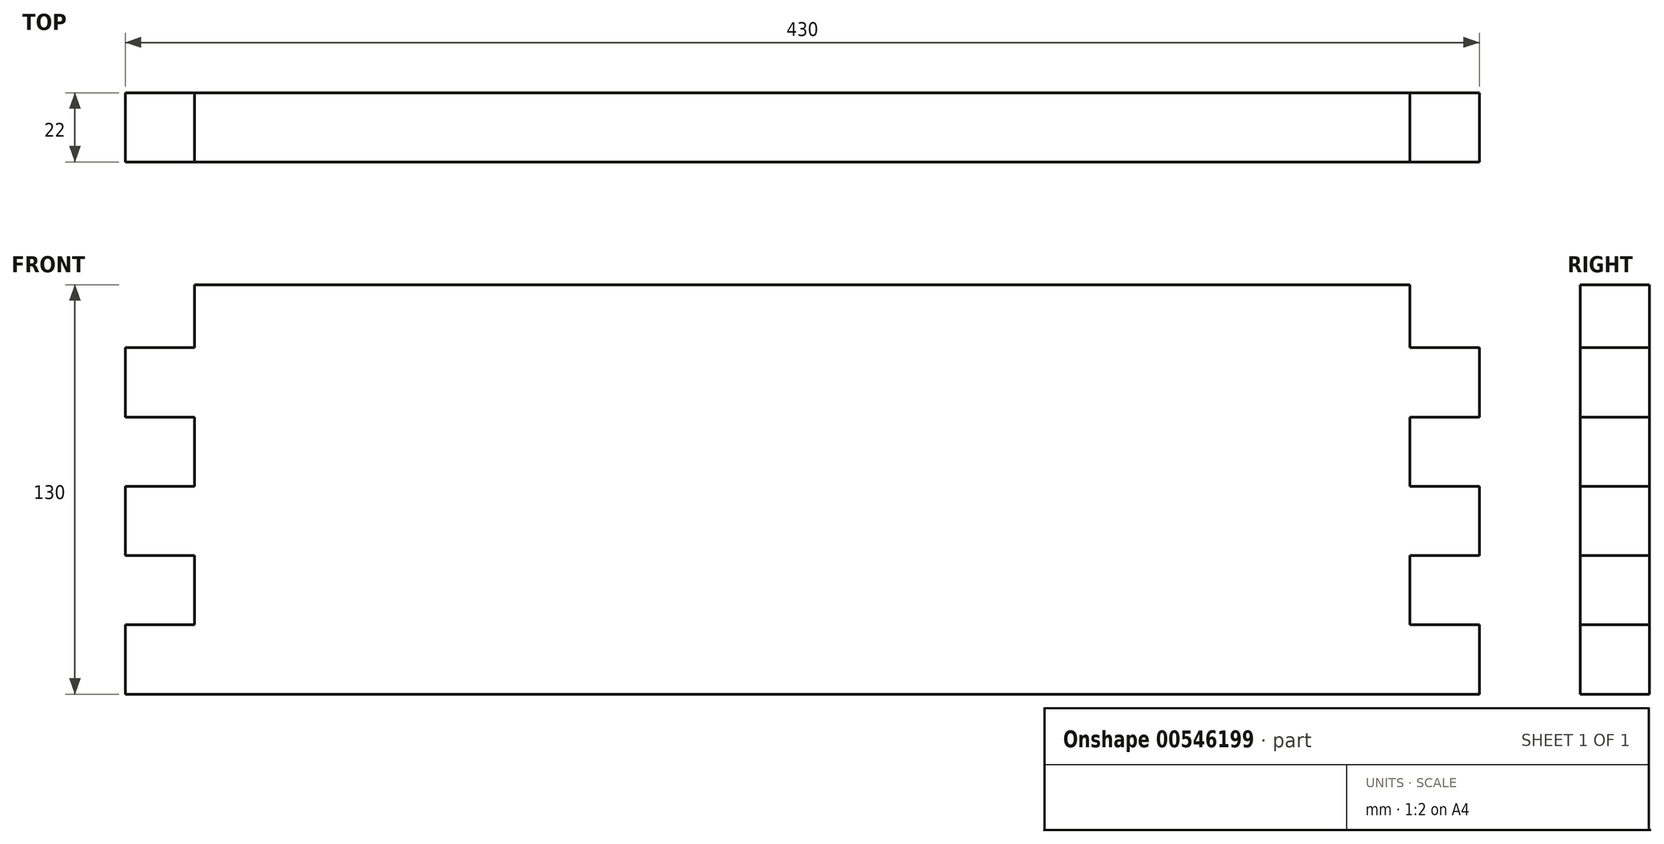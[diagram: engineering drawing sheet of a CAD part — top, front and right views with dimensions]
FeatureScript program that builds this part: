
annotation { "Feature Type Name" : "Feature", "Feature Type Description" : "" }
export const myFeature = defineFeature(function(context is Context, id is Id, definition is map)
    precondition{}
    {
        {
            var Q0;
            Q0=qCreatedBy(makeId("Front.planeOp"),FACE);
            var sketch = newSketch(context, id + "F0", { "sketchPlane" : qUnion([Q0])});
            skLineSegment(sketch, "E0.bottom", {"start": v(0, 0) * mm, "end": v(430, 0) * mm});
            skLineSegment(sketch, "E0.top", {"start": v(0, 130) * mm, "end": v(430, 130) * mm});
            skLineSegment(sketch, "E0.left", {"start": v(0, 0) * mm, "end": v(0, 130) * mm});
            skLineSegment(sketch, "E0.right", {"start": v(430, 0) * mm, "end": v(430, 130) * mm});
            skSolve(sketch);
        }
        {
            var Q0;
            Q0=makeQuery(id+"F0.imprint","IMPRINT",FACE,{"disambiguationData":[TD([[makeQuery(id+"F0.imprint","IMPRINT",EDGE,{"derivedFrom":sQuery(id+"F0.wireOp",EDGE,"E0.bottom")}),1.0]])]});
            extrude(context, id + "F1", {"entities" : qUnion([Q0]), "depth" : 22 * mm, "offsetDistance" : 25 * mm});
        }
        {
            var Q0;
            Q0=makeQuery(id+"F1.opExtrude","CAP_FACE",FACE,{"disambiguationData":[OSD([sQuery(id+"F0.wireOp",EDGE,"E0.bottom"),sQuery(id+"F0.wireOp",EDGE,"E0.top"),sQuery(id+"F0.wireOp",EDGE,"E0.left"),sQuery(id+"F0.wireOp",EDGE,"E0.right")])],"isStart":false});
            var sketch = newSketch(context, id + "F2", { "sketchPlane" : qUnion([Q0])});
            skLineSegment(sketch, "E1", {"start": v(215, 130) * mm, "end": v(215, 0) * mm});
            skLineSegment(sketch, "E2.bottom", {"start": v(0, 0) * mm, "end": v(22, 0) * mm});
            skLineSegment(sketch, "E2.top", {"start": v(0, 22) * mm, "end": v(22, 22) * mm});
            skLineSegment(sketch, "E2.left", {"start": v(0, 0) * mm, "end": v(0, 22) * mm});
            skLineSegment(sketch, "E2.right", {"start": v(22, 0) * mm, "end": v(22, 22) * mm});
            skLineSegment(sketch, "E3.top", {"start": v(0, 44) * mm, "end": v(22, 44) * mm});
            skLineSegment(sketch, "E3.left", {"start": v(0, 22) * mm, "end": v(0, 44) * mm});
            skLineSegment(sketch, "E3.right", {"start": v(22, 22) * mm, "end": v(22, 44) * mm});
            skLineSegment(sketch, "E4.top", {"start": v(0, 66) * mm, "end": v(22, 66) * mm});
            skLineSegment(sketch, "E4.left", {"start": v(0, 44) * mm, "end": v(0, 66) * mm});
            skLineSegment(sketch, "E4.right", {"start": v(22, 44) * mm, "end": v(22, 66) * mm});
            skLineSegment(sketch, "E5.top", {"start": v(0, 88) * mm, "end": v(22, 88) * mm});
            skLineSegment(sketch, "E5.left", {"start": v(0, 66) * mm, "end": v(0, 88) * mm});
            skLineSegment(sketch, "E5.right", {"start": v(22, 66) * mm, "end": v(22, 88) * mm});
            skLineSegment(sketch, "E6.top", {"start": v(0, 110) * mm, "end": v(22, 110) * mm});
            skLineSegment(sketch, "E6.left", {"start": v(0, 88) * mm, "end": v(0, 110) * mm});
            skLineSegment(sketch, "E6.right", {"start": v(22, 88) * mm, "end": v(22, 110) * mm});
            skLineSegment(sketch, "E7.MirrorCS", {"start": v(430, 22) * mm, "end": v(408, 22) * mm});
            skLineSegment(sketch, "E8.MirrorCS", {"start": v(430, 44) * mm, "end": v(408, 44) * mm});
            skLineSegment(sketch, "E9.MirrorCS", {"start": v(430, 66) * mm, "end": v(408, 66) * mm});
            skLineSegment(sketch, "E10.MirrorCS", {"start": v(430, 88) * mm, "end": v(408, 88) * mm});
            skLineSegment(sketch, "E11.MirrorCS", {"start": v(408, 66) * mm, "end": v(408, 88) * mm});
            skLineSegment(sketch, "E12.MirrorCS", {"start": v(408, 0) * mm, "end": v(408, 22) * mm});
            skLineSegment(sketch, "E13.MirrorCS", {"start": v(430, 0) * mm, "end": v(430, 22) * mm});
            skLineSegment(sketch, "E14.MirrorCS", {"start": v(430, 0) * mm, "end": v(408, 0) * mm});
            skLineSegment(sketch, "E15.MirrorCS", {"start": v(430, 22) * mm, "end": v(430, 44) * mm});
            skLineSegment(sketch, "E16.MirrorCS", {"start": v(408, 22) * mm, "end": v(408, 44) * mm});
            skLineSegment(sketch, "E17.MirrorCS", {"start": v(430, 66) * mm, "end": v(430, 88) * mm});
            skLineSegment(sketch, "E18.MirrorCS", {"start": v(430, 44) * mm, "end": v(430, 66) * mm});
            skLineSegment(sketch, "E19.MirrorCS", {"start": v(408, 44) * mm, "end": v(408, 66) * mm});
            skLineSegment(sketch, "E20.MirrorCS", {"start": v(408, 88) * mm, "end": v(408, 110) * mm});
            skLineSegment(sketch, "E21.MirrorCS", {"start": v(430, 110) * mm, "end": v(408, 110) * mm});
            skLineSegment(sketch, "E22.MirrorCS", {"start": v(430, 88) * mm, "end": v(430, 110) * mm});
            skLineSegment(sketch, "E23", {"start": v(22, 110) * mm, "end": v(22, 130) * mm});
            skLineSegment(sketch, "E24", {"start": v(408, 110) * mm, "end": v(408, 130) * mm});
            skSolve(sketch);
        }
        {
            var Q0;
            Q0=makeQuery(id+"F2.imprint","IMPRINT",FACE,{"disambiguationData":[TD([[makeQuery(id+"F2.imprint","IMPRINT",EDGE,{"derivedFrom":sQuery(id+"F2.wireOp",EDGE,"E2.top")}),1.0]])]});
            var Q1;
            Q1=makeQuery(id+"F2.imprint","IMPRINT",FACE,{"disambiguationData":[TD([[makeQuery(id+"F2.imprint","IMPRINT",EDGE,{"derivedFrom":sQuery(id+"F2.wireOp",EDGE,"E4.top")}),1.0]])]});
            var Q2;
            Q2=makeQuery(id+"F2.imprint","IMPRINT",FACE,{"disambiguationData":[TD([[makeQuery(id+"F2.imprint","IMPRINT",EDGE,{"derivedFrom":sQuery(id+"F2.wireOp",EDGE,"E11.MirrorCS")}),-1.0]])]});
            var Q3;
            Q3=makeQuery(id+"F2.imprint","IMPRINT",FACE,{"disambiguationData":[TD([[makeQuery(id+"F2.imprint","IMPRINT",EDGE,{"derivedFrom":sQuery(id+"F2.wireOp",EDGE,"E7.MirrorCS")}),-1.0]])]});
            var Q4;
            {var subQ0=sQuery(id+"F2.wireOp",EDGE,"E6.top");Q4=makeQuery(id+"F2.imprint","IMPRINT",FACE,{"disambiguationData":[TD([[makeQuery(id+"F2.imprint","IMPRINT",EDGE,{"derivedFrom":subQ0}),1.0]])]});}
            var Q5;
            {var subQ0=sQuery(id+"F2.wireOp",EDGE,"E21.MirrorCS");Q5=makeQuery(id+"F2.imprint","IMPRINT",FACE,{"disambiguationData":[TD([[makeQuery(id+"F2.imprint","IMPRINT",EDGE,{"derivedFrom":subQ0}),-1.0]])]});}
            extrude(context, id + "F3", {"entities" : qUnion([Q0, Q1, Q2, Q3, Q4, Q5]), "operationType" : NewBodyOperationType.REMOVE, "oppositeDirection" : true, "depth" : 25 * mm, "offsetDistance" : 25 * mm});
        }
    });
